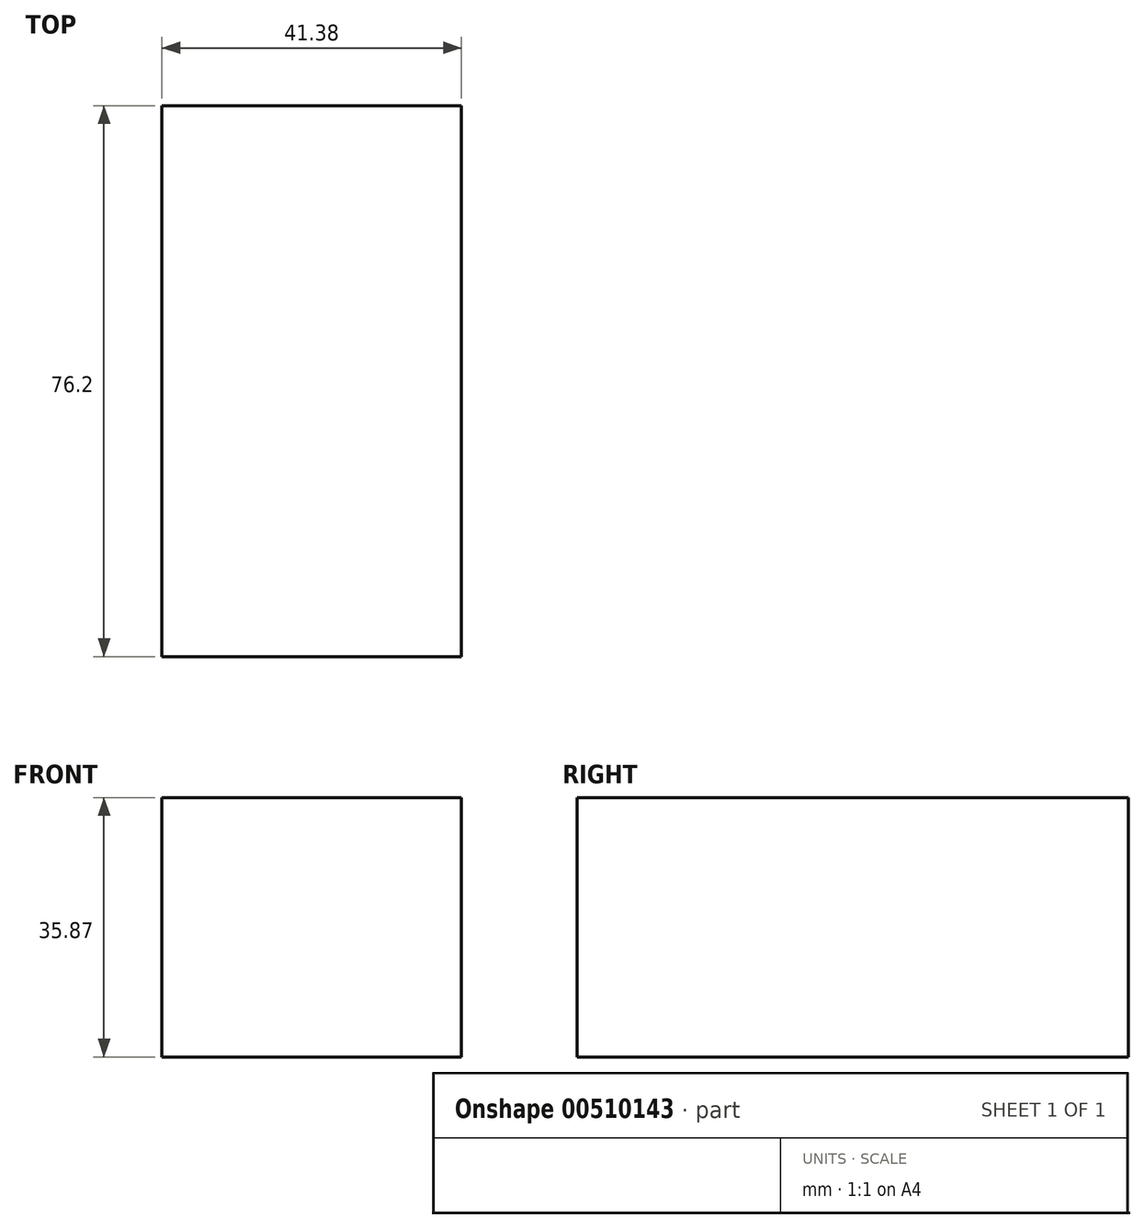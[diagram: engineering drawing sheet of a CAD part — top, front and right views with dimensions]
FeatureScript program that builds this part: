
annotation { "Feature Type Name" : "Feature", "Feature Type Description" : "" }
export const myFeature = defineFeature(function(context is Context, id is Id, definition is map)
    precondition{}
    {
        {
            var Q0;
            Q0=qCreatedBy(makeId("Front.planeOp"),FACE);
            var sketch = newSketch(context, id + "F0", { "sketchPlane" : qUnion([Q0])});
            skLineSegment(sketch, "E0.bottom", {"start": v(0, 0) * mm, "end": v(41.38, 0) * mm});
            skLineSegment(sketch, "E0.top", {"start": v(0, 35.87) * mm, "end": v(41.38, 35.87) * mm});
            skLineSegment(sketch, "E0.left", {"start": v(0, 0) * mm, "end": v(0, 35.87) * mm});
            skLineSegment(sketch, "E0.right", {"start": v(41.38, 0) * mm, "end": v(41.38, 35.87) * mm});
            skSolve(sketch);
        }
        {
            var Q0;
            Q0=makeQuery(id+"F0.imprint","IMPRINT",FACE,{"disambiguationData":[TD([[makeQuery(id+"F0.imprint","IMPRINT",EDGE,{"derivedFrom":sQuery(id+"F0.wireOp",EDGE,"E0.bottom")}),1.0]])]});
            extrude(context, id + "F1", {"entities" : qUnion([Q0]), "depth" : 76.2 * mm});
        }
    });
